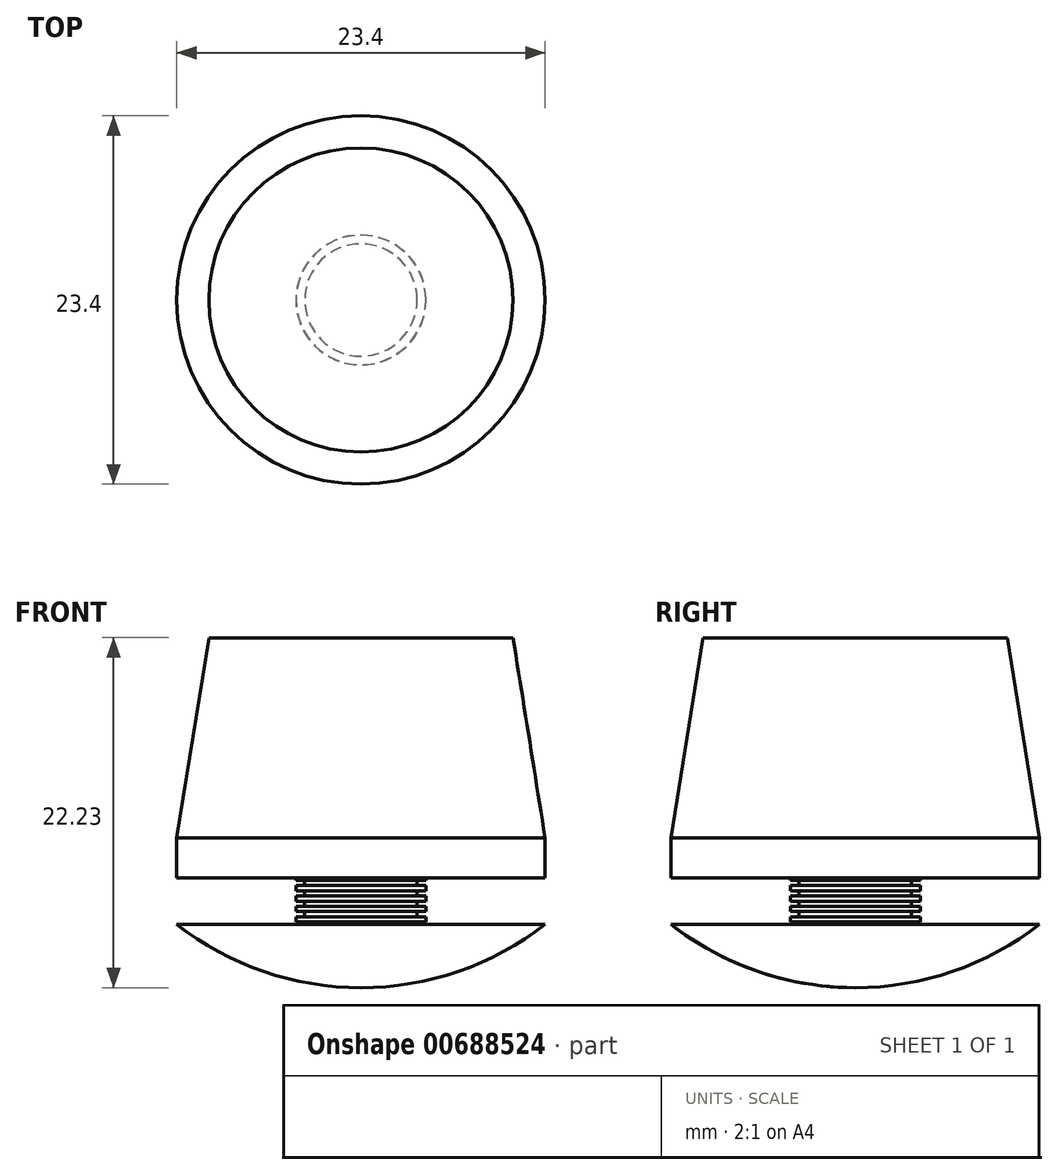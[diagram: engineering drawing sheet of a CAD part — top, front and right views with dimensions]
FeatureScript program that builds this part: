
annotation { "Feature Type Name" : "Feature", "Feature Type Description" : "" }
export const myFeature = defineFeature(function(context is Context, id is Id, definition is map)
    precondition{}
    {
        {
            var Q0;
            Q0=qCreatedBy(makeId("Right.planeOp"),FACE);
            var sketch = newSketch(context, id + "F0", { "sketchPlane" : qUnion([Q0])});
            skLineSegment(sketch, "E0", {"start": v(0, 0) * mm, "end": v(0, 38.1) * mm});
            skArc(sketch, "E1", {"start": v(-11.7, 4.02) * mm, "mid": v(-6.18, 1.03) * mm, "end": v(0, 0) * mm});
            skLineSegment(sketch, "E2", {"start": v(0, 0) * mm, "end": v(0, 19.05) * mm});
            skLineSegment(sketch, "E3", {"start": v(0, 0) * mm, "end": v(0, 9.53) * mm});
            skLineSegment(sketch, "E4", {"start": v(0, 9.53) * mm, "end": v(0, 4.76) * mm});
            skLineSegment(sketch, "E5", {"start": v(-9.66, 22.23) * mm, "end": v(0, 22.23) * mm});
            skLineSegment(sketch, "E6", {"start": v(-11.7, 4.02) * mm, "end": v(-3.57, 4.02) * mm});
            skLineSegment(sketch, "E7", {"start": v(-11.7, 9.53) * mm, "end": v(-11.7, 6.98) * mm});
            skLineSegment(sketch, "E8", {"start": v(-11.7, 6.98) * mm, "end": v(-4.13, 6.98) * mm});
            skLineSegment(sketch, "E9", {"start": v(-11.7, 9.52) * mm, "end": v(-9.66, 22.23) * mm});
            skPoint(sketch, "E10.orphan", {"position": v(-11.7, 22.23) * mm});
            skLineSegment(sketch, "E11", {"start": v(0, 22.23) * mm, "end": v(0, 0) * mm});
            skLineSegment(sketch, "E12.0", {"start": v(-3.57, 6.81) * mm, "end": v(-3.57, 6.48) * mm});
            skLineSegment(sketch, "E13.0", {"start": v(-4.13, 6.15) * mm, "end": v(-4.13, 6.48) * mm});
            skLineSegment(sketch, "E14.0", {"start": v(-3.57, 6.15) * mm, "end": v(-3.57, 5.82) * mm});
            skLineSegment(sketch, "E15.0", {"start": v(-4.13, 5.5) * mm, "end": v(-4.13, 5.82) * mm});
            skLineSegment(sketch, "E16.0", {"start": v(-3.57, 5.5) * mm, "end": v(-3.57, 5.16) * mm});
            skLineSegment(sketch, "E17.0", {"start": v(-4.13, 4.84) * mm, "end": v(-4.13, 5.16) * mm});
            skLineSegment(sketch, "E18.0", {"start": v(-3.57, 4.84) * mm, "end": v(-3.57, 4.5) * mm});
            skLineSegment(sketch, "E19.0", {"start": v(-4.12, 4.5) * mm, "end": v(-4.12, 4.18) * mm});
            skLineSegment(sketch, "E20.0", {"start": v(-3.57, 4.18) * mm, "end": v(-3.57, 4.02) * mm});
            skLineSegment(sketch, "E21.0", {"start": v(-4.13, 6.81) * mm, "end": v(-4.13, 6.98) * mm});
            skLineSegment(sketch, "E22", {"start": v(-4.13, 6.81) * mm, "end": v(-3.57, 6.81) * mm});
            skLineSegment(sketch, "E23", {"start": v(-4.13, 6.48) * mm, "end": v(-3.57, 6.48) * mm});
            skLineSegment(sketch, "E24", {"start": v(-4.13, 6.15) * mm, "end": v(-3.57, 6.15) * mm});
            skLineSegment(sketch, "E25", {"start": v(-4.13, 5.82) * mm, "end": v(-3.57, 5.82) * mm});
            skLineSegment(sketch, "E26", {"start": v(-4.13, 5.5) * mm, "end": v(-3.57, 5.5) * mm});
            skLineSegment(sketch, "E27", {"start": v(-4.13, 5.16) * mm, "end": v(-3.57, 5.16) * mm});
            skLineSegment(sketch, "E28", {"start": v(-4.13, 4.84) * mm, "end": v(-3.57, 4.84) * mm});
            skLineSegment(sketch, "E29", {"start": v(-4.12, 4.5) * mm, "end": v(-3.57, 4.5) * mm});
            skLineSegment(sketch, "E30", {"start": v(-4.12, 4.18) * mm, "end": v(-3.57, 4.18) * mm});
            skSolve(sketch);
        }
        {
            var Q0;
            Q0 = qSketchRegion(id + "F0", true);
            var Q1;
            Q1=sQuery(id+"F0.wireOp",EDGE,"E11");
            revolve(context, id + "F1", {"entities" : qUnion([Q0]), "axis" : qUnion([Q1]), "revolveType" : RevolveType.FULL});
        }
    });
